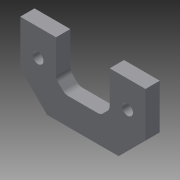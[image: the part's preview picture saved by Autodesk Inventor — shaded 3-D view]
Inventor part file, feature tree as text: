
AUTODESK INVENTOR PART (.ipt)
format: ipt  version: 2013 (Build 170138000, 138)  size: 118,272 bytes
history: native  units: mm
features: extrude x1, fillet x1, sketch x1
ambient origin geometry x8: Origin, YZ Plane, XZ Plane, XY Plane, X Axis, Y Axis, Z Axis, Center Point
feature tree (3):
  extrude  "押し出し2"  Depth=20.0mm
  fillet  "フィレット2"  Radius=10.0mm
  sketch  "スケッチ1"
